# Revit family: Screens-Mounted-Teknion-JNSEFB-Fabric_Elevated-R2015
name_source: partatom
category: Furniture
revit_build: Autodesk Revit Architecture 2015 (Build: 20140323_1530(x64)
units: mm (PartAtom-declared; Revit-internal decimal feet)

## types (4) — shared parameters
Assembly Code = E2020200
Manufacturer = Teknion
Manufacturer Fax = 416.661.4586
Part Number = JNSEFB
Product Documentation Link = http://www.teknion.com
Product Line = Expansion Cityline
Product Page URL = http://www.teknion.com
Series = Expansion Cityline
Sustainability Data = http://www.teknion.com
URL = www.teknion.com
Unit Weight URL = http://www.teknion.com
Warranty = http://www.teknion.com

## per-type parameters (varying)
| type | Both Side | Description | Model | Side A | Side B |
| Standard Width | No | Fabric Elevated Screen - Beam Mounted, 10" Modesty Base, Standard Width | JNSEFB10__S | No | No |
| One Side - Left | No | Fabric Elevated Screen - Beam Mounted, 10" Modesty Base, Left Side Width Extension | JNSEFB10__L | Yes | No |
| Both Side | Yes | Fabric Elevated Screen - Beam Mounted, 10" Modesty Base, Both Sides Width Extension | JNSEFB10__B | No | No |
| One Side - Right | No | Fabric Elevated Screen - Beam Mounted, 10" Modesty Base, Right Side Width Extension | JNSEFB10__R | No | Yes |

type visibility flags (boolean, named after types; folded from table):
- Standard Width: Yes: Standard Width
- One Side - Left: Yes: (none)
- Both Side: Yes: (none)
- One Side - Right: Yes: (none)

## geometry (parser evidence)
native form markers: Sweep x2
no freeform markers — native parametric forms only
